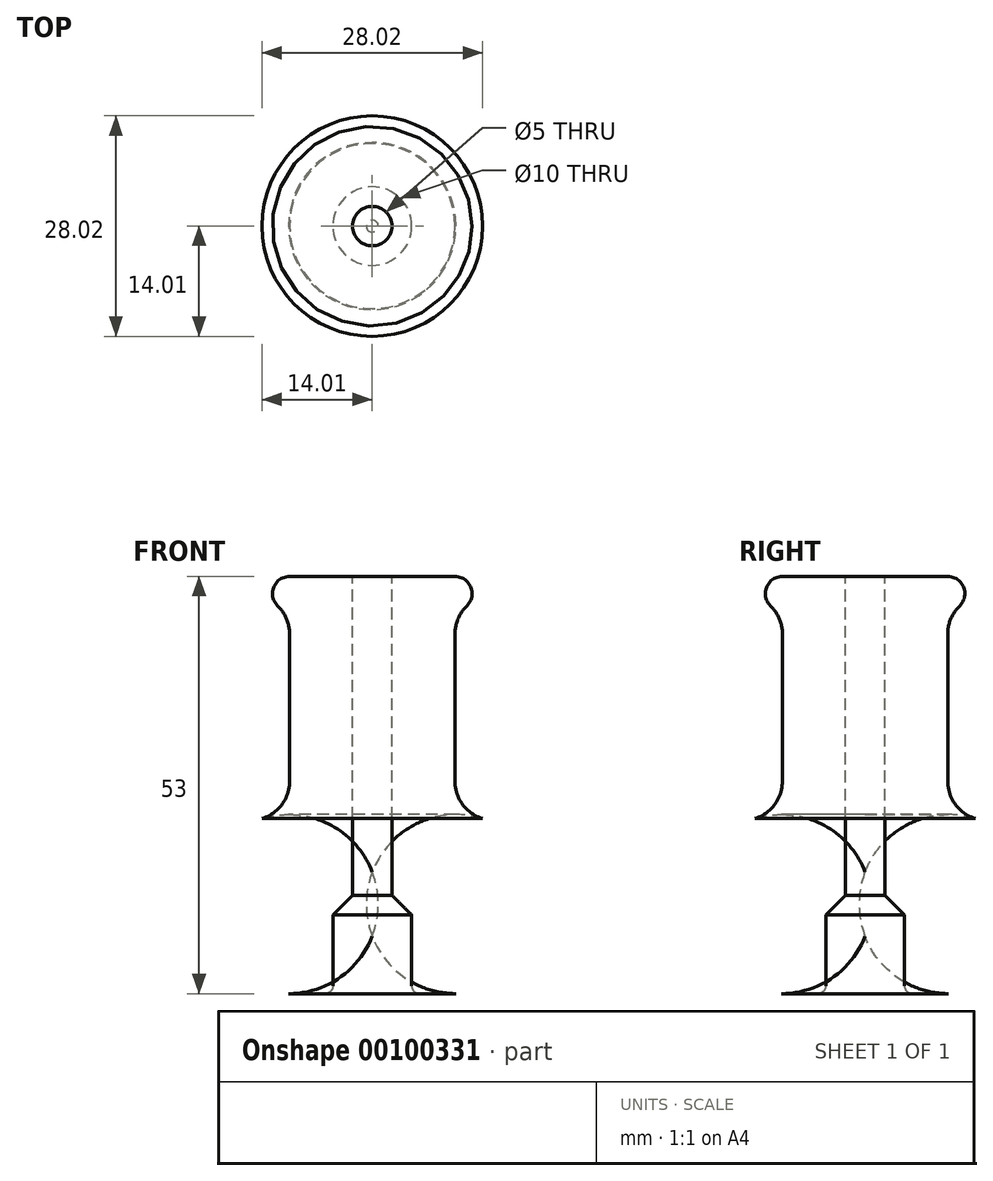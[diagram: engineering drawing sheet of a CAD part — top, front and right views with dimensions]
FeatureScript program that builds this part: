
annotation { "Feature Type Name" : "Feature", "Feature Type Description" : "" }
export const myFeature = defineFeature(function(context is Context, id is Id, definition is map)
    precondition{}
    {
        {
            var Q0;
            Q0=qCreatedBy(makeId("Front.planeOp"),FACE);
            var sketch = newSketch(context, id + "F0", { "sketchPlane" : qUnion([Q0])});
            skLineSegment(sketch, "E0", {"start": v(0, 27.25) * mm, "end": v(0, -32.75) * mm, "construction": true});
            skLineSegment(sketch, "E1", {"start": v(0, 27.25) * mm, "end": v(-2.5, 27.25) * mm, "construction": true});
            skLineSegment(sketch, "E2", {"start": v(-2.5, 27.25) * mm, "end": v(-2.5, 30.25) * mm});
            skLineSegment(sketch, "E3", {"start": v(-5, -12.75) * mm, "end": v(-5, -21.75) * mm});
            skLineSegment(sketch, "E4", {"start": v(-2.5, 30.25) * mm, "end": v(-10.5, 30.25) * mm});
            skArc(sketch, "E5", {"start": v(-10.5, 30.25) * mm, "mid": v(-12.52, 28.9) * mm, "end": v(-12.02, 26.51) * mm});
            skLineSegment(sketch, "E6", {"start": v(-10.5, 22.93) * mm, "end": v(-10.5, 4.25) * mm});
            skLineSegment(sketch, "E7", {"start": v(-5, -12.75) * mm, "end": v(-2.5, -10.25) * mm});
            skLineSegment(sketch, "E8", {"start": v(-2.5, 27.25) * mm, "end": v(-2.5, -10.25) * mm});
            skLineSegment(sketch, "E9", {"start": v(-6, -22.75) * mm, "end": v(-10.61, -22.75) * mm});
            skArc(sketch, "E10", {"start": v(-14, -0.52) * mm, "mid": v(-21.86, -13.09) * mm, "end": v(-10.61, -22.75) * mm});
            skPoint(sketch, "E11.visualSharp", {"position": v(-10.5, 0) * mm});
            skArc(sketch, "E11.filletArc", {"start": v(-14, -0.52) * mm, "mid": v(-11.47, 1.3) * mm, "end": v(-10.5, 4.25) * mm});
            skPoint(sketch, "E12.visualSharp", {"position": v(-10.5, 25.9) * mm});
            skArc(sketch, "E12.filletArc", {"start": v(-10.5, 22.93) * mm, "mid": v(-10.9, 24.87) * mm, "end": v(-12.02, 26.51) * mm});
            skPoint(sketch, "E13.visualSharp", {"position": v(-5, -22.75) * mm});
            skArc(sketch, "E13.filletArc", {"start": v(-6, -22.75) * mm, "mid": v(-5.3, -22.45) * mm, "end": v(-5, -21.75) * mm});
            skSolve(sketch);
        }
        {
            var Q0;
            Q0=makeQuery(id+"F0.imprint","IMPRINT",FACE,{"disambiguationData":[TD([[makeQuery(id+"F0.imprint","IMPRINT",EDGE,{"derivedFrom":sQuery(id+"F0.wireOp",EDGE,"E2")}),1.0]])]});
            var Q1;
            Q1=sQuery(id+"F0.wireOp",EDGE,"E0");
            revolve(context, id + "F1", {"entities" : qUnion([Q0]), "axis" : qUnion([Q1]), "revolveType" : RevolveType.FULL});
        }
    });
